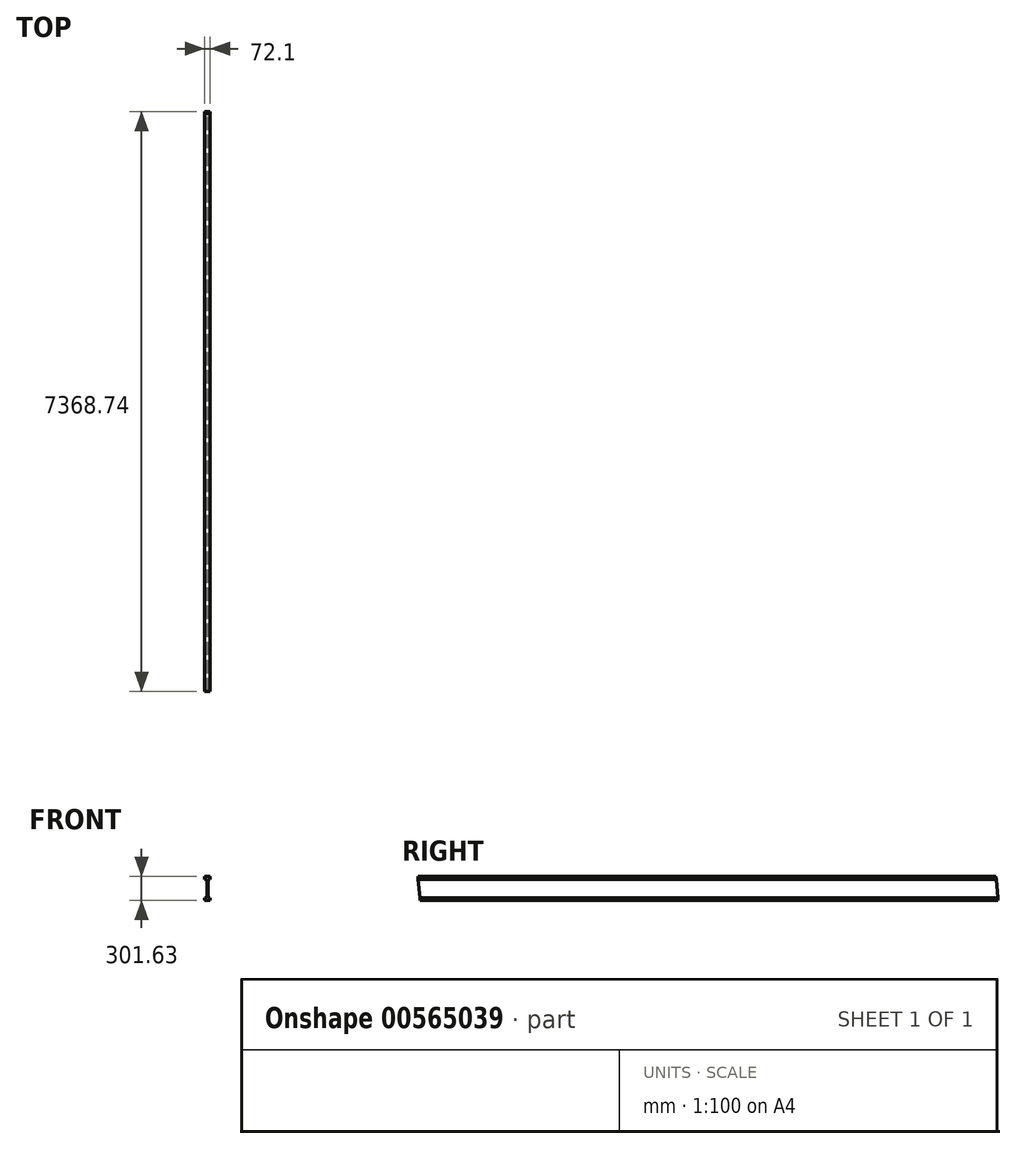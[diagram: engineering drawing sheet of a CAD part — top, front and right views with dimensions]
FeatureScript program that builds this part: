
annotation { "Feature Type Name" : "Feature", "Feature Type Description" : "" }
export const myFeature = defineFeature(function(context is Context, id is Id, definition is map)
    precondition{}
    {
        {
            var Q0;
            Q0=qCreatedBy(makeId("Front.planeOp"),FACE);
            var sketch = newSketch(context, id + "F0", { "sketchPlane" : qUnion([Q0])});
            skLineSegment(sketch, "E0", {"start": v(0, 0) * mm, "end": v(0, 33.65) * mm});
            skLineSegment(sketch, "E1", {"start": v(0, 33.65) * mm, "end": v(31.29, 33.65) * mm});
            skLineSegment(sketch, "E2", {"start": v(31.29, 33.65) * mm, "end": v(31.29, 267.97) * mm});
            skLineSegment(sketch, "E3", {"start": v(31.29, 267.97) * mm, "end": v(0, 267.97) * mm});
            skLineSegment(sketch, "E4", {"start": v(0, 267.97) * mm, "end": v(0, 301.63) * mm});
            skLineSegment(sketch, "E5", {"start": v(0, 301.63) * mm, "end": v(72.1, 301.63) * mm});
            skLineSegment(sketch, "E6", {"start": v(72.1, 301.63) * mm, "end": v(72.1, 267.97) * mm});
            skLineSegment(sketch, "E7", {"start": v(72.1, 267.97) * mm, "end": v(40.81, 267.97) * mm});
            skLineSegment(sketch, "E8", {"start": v(40.81, 267.97) * mm, "end": v(40.81, 33.65) * mm});
            skLineSegment(sketch, "E9", {"start": v(40.81, 33.65) * mm, "end": v(72.1, 33.66) * mm});
            skLineSegment(sketch, "E10", {"start": v(72.1, 33.66) * mm, "end": v(72.1, 0) * mm});
            skLineSegment(sketch, "E11", {"start": v(72.1, 0) * mm, "end": v(0, 0) * mm});
            skSolve(sketch);
        }
        {
            var Q0;
            Q0=qSketchRegion(id+"F0",true);
            extrude(context, id + "F1", {"entities" : qUnion([Q0]), "depth" : 7620 * mm});
        }
        {
            var Q0;
            Q0=makeQuery(id+"F1.opExtrude","SWEPT_FACE",FACE,{"disambiguationData":[OSD([sQuery(id+"F0.wireOp",EDGE,"E10")])]});
            var sketch = newSketch(context, id + "F2", { "sketchPlane" : qUnion([Q0])});
            skLineSegment(sketch, "E12", {"start": v(-140.22, 0) * mm, "end": v(-7149.76, -607.32) * mm, "construction": true});
            skLineSegment(sketch, "E13", {"start": v(-7149.76, -607.32) * mm, "end": v(-7202.38, 0) * mm, "construction": true});
            skLineSegment(sketch, "E14", {"start": v(-7202.38, 0) * mm, "end": v(-7342.6, 0) * mm, "construction": true});
            skLineSegment(sketch, "E15", {"start": v(-7342.6, 0) * mm, "end": v(-7368.74, 301.62) * mm});
            skLineSegment(sketch, "E16", {"start": v(-140.22, 0) * mm, "end": v(0, 0) * mm, "construction": true});
            skLineSegment(sketch, "E17", {"start": v(0, 0) * mm, "end": v(-26.13, 301.63) * mm});
            skLineSegment(sketch, "E18", {"start": v(-26.13, 301.63) * mm, "end": v(-7368.74, 301.62) * mm, "construction": true});
            skLineSegment(sketch, "E19", {"start": v(-7368.74, 301.62) * mm, "end": v(-7620, 301.62) * mm});
            skLineSegment(sketch, "E20", {"start": v(-7620, 301.63) * mm, "end": v(-7620, 0) * mm});
            skLineSegment(sketch, "E21", {"start": v(-7620, 0) * mm, "end": v(-7342.6, 0) * mm});
            skLineSegment(sketch, "E22", {"start": v(0, 0) * mm, "end": v(0, 301.63) * mm});
            skLineSegment(sketch, "E23", {"start": v(0, 301.63) * mm, "end": v(-26.13, 301.63) * mm});
            skSolve(sketch);
        }
        {
            var Q0;
            Q0 = qSketchRegion(id + "F2", true);
            extrude(context, id + "F3", {"entities" : qUnion([Q0]), "operationType" : NewBodyOperationType.REMOVE, "endBound" : BoundingType.THROUGH_ALL, "oppositeDirection" : true, "depth" : 25.4 * mm, "offsetDistance" : 25.4 * mm});
        }
    });
